# Revit family: NBS_CordekLtd_DschrgeAndVntltngStackTrmntns_RectangularGulleyVent-CGV-024
name_source: partatom
category: Specialty Equipment
revit_build: Autodesk Revit 2014 (Build: 20131024_2115(x64)
units: mm (PartAtom-declared; Revit-internal decimal feet)

## types (1)
- CGV-024
    Arrangement = Gulley vent with slotted lid
    AssetType = Fixed
    BIMObjectName = NBS_CordekLtd_DischargeAndVentilatingStackTerminations_RectangularGulleyVent-CGV-024
    Category = Pr_65_52_61_23:Discharge and ventilating stack terminations
    ConnectionSizes = Gas inlet: 110 mm; Water outlet: 175 mm
    Description = Gulley vent with stainless steel slotted lid
    DurationUnit = year
    Features = Base connection to stormwater collection, land drainage or soakaway system
    FreeAirFlow = 18100 mm²
    GulleyVentLidMaterial = NBS_Concept_GulleySlotted
    GulleyVentMaterial = NBS_Concept
    Height = 690 mm
    IfcExportAs = IfcStackTerminalType
    IfcExportType = NOTDEFINED
    Length = 412 mm
    ManufacturerName = Cordek Ltd
    ManufacturerURL = www.cordek.com
    Material = Lid: Stainless steel
    ModelNumber = CGV-024
    ModelReference = Rectangular Gulley Vent - CGV-024
    NBSCertification = http://www.nationalbimlibrary.com
    NBSDescription = Discharge and ventilating stack terminations
    NBSReference = 90-10-60/437
    Name = DischargeAndVentilatingStackTerminations_RectangularGulleyVent-CGV-024_CordekLtd
    NominalHeight = 690 mm
    NominalLength = 412 mm
    NominalWidth = 212 mm
    ProductInformation = www.cordek.com/uploads/data_sheets/M-DS32_ground_level_vent_box_data_sheet_v2_cordek.pdf
    Shape = Rectangular
    Size = 410 x 210 x 690 mm
    Uniclass2 = 90-62-24/422
    Uniclass2015Description = Discharge and ventilating stack terminations
    Uniclass2015Reference = Pr_65_52_61_23
    Uniclass2015Version = Products v1.1
    Version = 1
    WarrantyDurationUnit = year
    Width = 212 mm

## geometry (parser evidence)
native form markers: Sweep x1
no freeform markers — native parametric forms only
